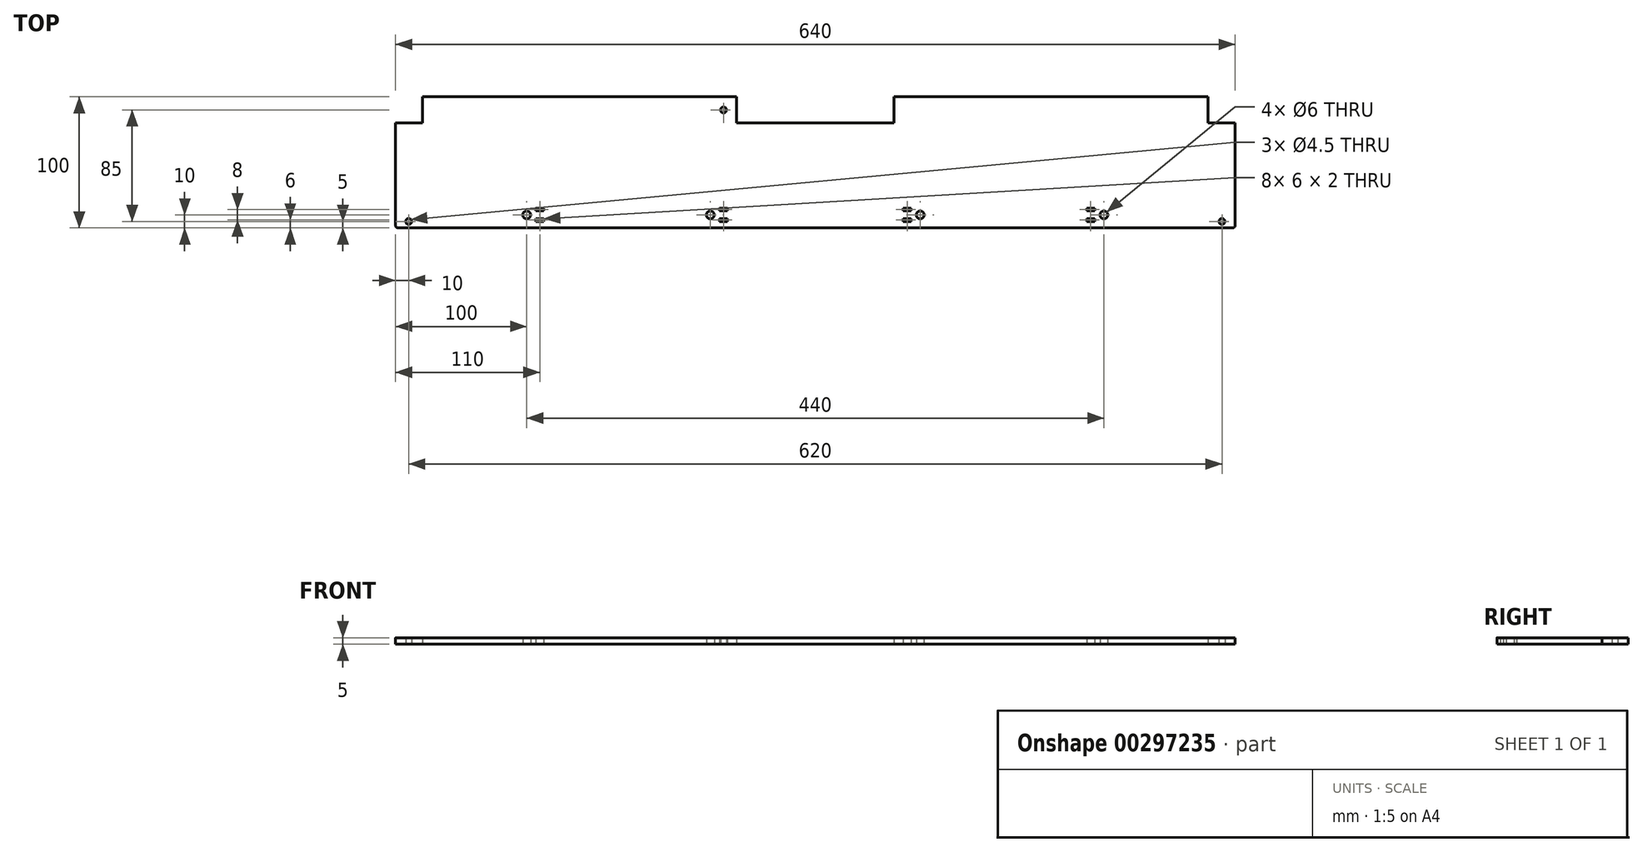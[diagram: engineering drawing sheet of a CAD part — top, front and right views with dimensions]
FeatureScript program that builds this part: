
annotation { "Feature Type Name" : "Feature", "Feature Type Description" : "" }
export const myFeature = defineFeature(function(context is Context, id is Id, definition is map)
    precondition{}
    {
        {
            var Q0;
            Q0=qCreatedBy(makeId("Top.planeOp"),FACE);
            var sketch = newSketch(context, id + "F0", { "sketchPlane" : qUnion([Q0])});
            skCircle(sketch, "E0", {"center": v(-70, 0) * mm, "radius": 3 * mm});
            skCircle(sketch, "E1.MirrorC", {"center": v(70, 0) * mm, "radius": 3 * mm});
            skCircle(sketch, "E2", {"center": v(230, 0) * mm, "radius": 3 * mm});
            skCircle(sketch, "E3.MirrorC", {"center": v(370, 0) * mm, "radius": 3 * mm});
            skLineSegment(sketch, "E4.bottom", {"start": v(-168, -10) * mm, "end": v(468, -10) * mm});
            skLineSegment(sketch, "E4.left", {"start": v(-170, -8) * mm, "end": v(-170, 70) * mm});
            skLineSegment(sketch, "E4.right", {"start": v(470, -8) * mm, "end": v(470, 70) * mm});
            skPoint(sketch, "E5.visualSharp", {"position": v(-170, -10) * mm});
            skArc(sketch, "E5.filletArc", {"start": v(-170, -8) * mm, "mid": v(-169.41, -9.41) * mm, "end": v(-168, -10) * mm});
            skPoint(sketch, "E6.visualSharp", {"position": v(470, -10) * mm});
            skArc(sketch, "E6.filletArc", {"start": v(468, -10) * mm, "mid": v(469.41, -9.41) * mm, "end": v(470, -8) * mm});
            skLineSegment(sketch, "E7", {"start": v(-149.5, 90) * mm, "end": v(90, 90) * mm});
            skLineSegment(sketch, "E8.top", {"start": v(-170, 70) * mm, "end": v(-149.5, 70) * mm});
            skLineSegment(sketch, "E8.right", {"start": v(-149.5, 90) * mm, "end": v(-149.5, 70) * mm});
            skLineSegment(sketch, "E9.top", {"start": v(470, 70) * mm, "end": v(449.5, 70) * mm});
            skLineSegment(sketch, "E9.right", {"start": v(449.5, 90) * mm, "end": v(449.5, 70) * mm});
            skLineSegment(sketch, "E10.top", {"start": v(210, 70) * mm, "end": v(90, 70) * mm});
            skLineSegment(sketch, "E10.left", {"start": v(210, 90) * mm, "end": v(210, 70) * mm});
            skLineSegment(sketch, "E10.right", {"start": v(90, 90) * mm, "end": v(90, 70) * mm});
            skPoint(sketch, "E10.middle", {"position": v(150, 80) * mm});
            skPoint(sketch, "E10.middle.positionSnap0", {"position": v(150, 90) * mm});
            skPoint(sketch, "E10.centerSnap0", {"position": v(150, 90) * mm});
            skPoint(sketch, "E11.orphan", {"position": v(-170, 90) * mm});
            skLineSegment(sketch, "E12.trimOffspring", {"start": v(210, 90) * mm, "end": v(449.5, 90) * mm});
            skPoint(sketch, "E13.orphan", {"position": v(470, 90) * mm});
            skCircle(sketch, "E14", {"center": v(-160, -5) * mm, "radius": 2.25 * mm});
            skCircle(sketch, "E15", {"center": v(460, -5) * mm, "radius": 2.25 * mm});
            skCircle(sketch, "E16", {"center": v(80, 80) * mm, "radius": 2.25 * mm});
            skLineSegment(sketch, "E17.bottom", {"start": v(-63, 5) * mm, "end": v(-57, 5) * mm});
            skLineSegment(sketch, "E17.top", {"start": v(-63, 3) * mm, "end": v(-57, 3) * mm});
            skLineSegment(sketch, "E17.left", {"start": v(-63, 5) * mm, "end": v(-63, 3) * mm});
            skLineSegment(sketch, "E17.right", {"start": v(-57, 5) * mm, "end": v(-57, 3) * mm});
            skLineSegment(sketch, "E18.bottom", {"start": v(-63, -3) * mm, "end": v(-57, -3) * mm});
            skLineSegment(sketch, "E18.top", {"start": v(-63, -5) * mm, "end": v(-57, -5) * mm});
            skLineSegment(sketch, "E18.left", {"start": v(-63, -3) * mm, "end": v(-63, -5) * mm});
            skLineSegment(sketch, "E18.right", {"start": v(-57, -3) * mm, "end": v(-57, -5) * mm});
            skLineSegment(sketch, "E19.bottom", {"start": v(77, 5) * mm, "end": v(83, 5) * mm});
            skLineSegment(sketch, "E19.top", {"start": v(77, 3) * mm, "end": v(83, 3) * mm});
            skLineSegment(sketch, "E19.left", {"start": v(77, 5) * mm, "end": v(77, 3) * mm});
            skLineSegment(sketch, "E19.right", {"start": v(83, 5) * mm, "end": v(83, 3) * mm});
            skLineSegment(sketch, "E20.bottom", {"start": v(77, -3) * mm, "end": v(83, -3) * mm});
            skLineSegment(sketch, "E20.top", {"start": v(77, -5) * mm, "end": v(83, -5) * mm});
            skLineSegment(sketch, "E20.left", {"start": v(77, -3) * mm, "end": v(77, -5) * mm});
            skLineSegment(sketch, "E20.right", {"start": v(83, -3) * mm, "end": v(83, -5) * mm});
            skPoint(sketch, "E21", {"position": v(-50, 0) * mm});
            skLineSegment(sketch, "E22.bottom", {"start": v(357, 5) * mm, "end": v(363, 5) * mm});
            skLineSegment(sketch, "E22.top", {"start": v(357, 3) * mm, "end": v(363, 3) * mm});
            skLineSegment(sketch, "E22.left", {"start": v(357, 5) * mm, "end": v(357, 3) * mm});
            skLineSegment(sketch, "E22.right", {"start": v(363, 5) * mm, "end": v(363, 3) * mm});
            skLineSegment(sketch, "E23.bottom", {"start": v(357, -3) * mm, "end": v(363, -3) * mm});
            skLineSegment(sketch, "E23.top", {"start": v(357, -5) * mm, "end": v(363, -5) * mm});
            skLineSegment(sketch, "E23.left", {"start": v(357, -3) * mm, "end": v(357, -5) * mm});
            skLineSegment(sketch, "E23.right", {"start": v(363, -3) * mm, "end": v(363, -5) * mm});
            skLineSegment(sketch, "E24.bottom", {"start": v(217, 5) * mm, "end": v(223, 5) * mm});
            skLineSegment(sketch, "E24.top", {"start": v(217, 3) * mm, "end": v(223, 3) * mm});
            skLineSegment(sketch, "E24.left", {"start": v(217, 5) * mm, "end": v(217, 3) * mm});
            skLineSegment(sketch, "E24.right", {"start": v(223, 5) * mm, "end": v(223, 3) * mm});
            skLineSegment(sketch, "E25.bottom", {"start": v(217, -3) * mm, "end": v(223, -3) * mm});
            skLineSegment(sketch, "E25.top", {"start": v(217, -5) * mm, "end": v(223, -5) * mm});
            skLineSegment(sketch, "E25.left", {"start": v(217, -3) * mm, "end": v(217, -5) * mm});
            skLineSegment(sketch, "E25.right", {"start": v(223, -3) * mm, "end": v(223, -5) * mm});
            skSolve(sketch);
        }
        {
            var Q0;
            Q0=makeQuery(id+"F0.imprint","IMPRINT",FACE,{"disambiguationData":[TD([[makeQuery(id+"F0.imprint","IMPRINT",EDGE,{"derivedFrom":sQuery(id+"F0.wireOp",EDGE,"E0")}),-1.0]])]});
            extrude(context, id + "F1", {"entities" : qUnion([Q0]), "depth" : 5 * mm});
        }
    });
